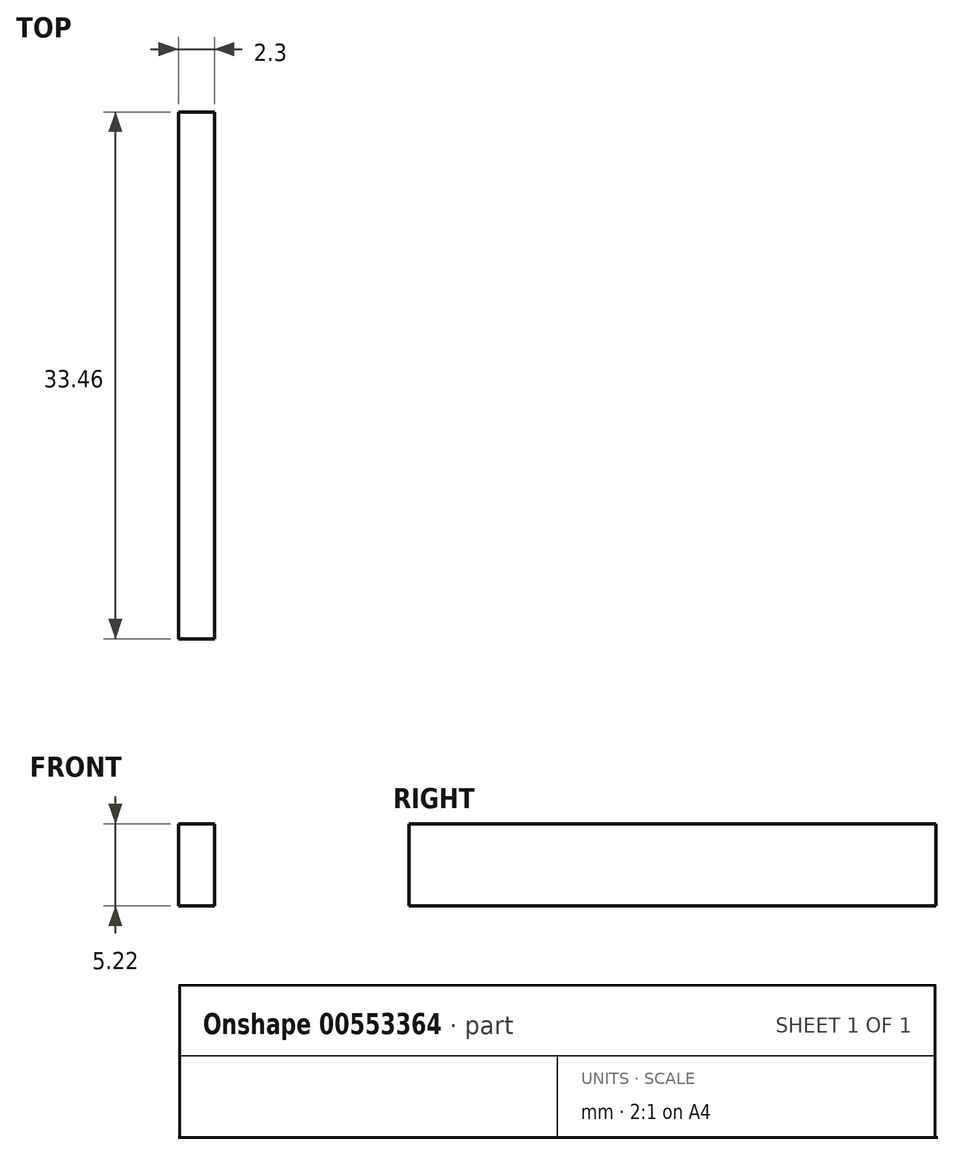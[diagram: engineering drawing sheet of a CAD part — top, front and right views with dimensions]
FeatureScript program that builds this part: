
annotation { "Feature Type Name" : "Feature", "Feature Type Description" : "" }
export const myFeature = defineFeature(function(context is Context, id is Id, definition is map)
    precondition{}
    {
        {
            var Q0;
            Q0=qCreatedBy(makeId("Right.planeOp"),FACE);
            var sketch = newSketch(context, id + "F0", { "sketchPlane" : qUnion([Q0])});
            skLineSegment(sketch, "E0.bottom", {"start": v(0, 0) * mm, "end": v(33.46, 0) * mm});
            skLineSegment(sketch, "E0.top", {"start": v(0, -5.22) * mm, "end": v(33.46, -5.22) * mm});
            skLineSegment(sketch, "E0.left", {"start": v(0, -5.22) * mm, "end": v(0, 0) * mm});
            skLineSegment(sketch, "E0.right", {"start": v(33.46, -5.22) * mm, "end": v(33.46, 0) * mm});
            skSolve(sketch);
        }
        {
            var Q0;
            Q0=makeQuery(id+"F0.imprint","IMPRINT",FACE,{"disambiguationData":[TD([[makeQuery(id+"F0.imprint","IMPRINT",EDGE,{"derivedFrom":sQuery(id+"F0.wireOp",EDGE,"E0.bottom")}),-1.0]])]});
            extrude(context, id + "F1", {"entities" : qUnion([Q0]), "depth" : 2.3 * mm, "offsetDistance" : 25 * mm});
        }
    });
